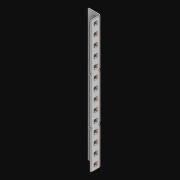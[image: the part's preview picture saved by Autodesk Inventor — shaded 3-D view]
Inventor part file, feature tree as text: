
AUTODESK INVENTOR PART (.ipt)
format: ipt  version: 2021 (Build 250183000, 183)  size: 1,149,440 bytes
history: native  units: in
note: dims shown in document units (in); Inventor stores cm internally (conversion verified against a paired STEP export)
features: extrude x30, other x28, sketch x4, pattern_linear x2, sheet_metal_op x1
ambient origin geometry x8: Origin, YZ Plane, XZ Plane, XY Plane, X Axis, Y Axis, Z Axis, Center Point
bodies: Solid1 (feature_tree)
feature tree (65):
  pattern_linear  "Rectangular Pattern1"  Spacing1=0.5in  [1 undecoded]
  pattern_linear  "Rectangular Pattern3"  Count1=14  [1 undecoded]
  extrude  "Extrusion1"  Depth=0.5in
  extrude  "Extrusion2"  Depth=0.5in
  sketch  "Sketch1"  dims[d0=0.182in]
  other  "Srf1"
  sketch  "Sketch3"  dims[d1=0.063in d2=0.0in]
  other  "Srf3"
  other  "Srf4"
  other  "Srf5"
  other  "Srf6"
  other  "Srf7"
  other  "Srf8"
  other  "Srf9"
  other  "Srf10"
  other  "Srf11"
  other  "Srf12"
  other  "Srf13"
  other  "Srf14"
  other  "Srf15"
  other  "Srf16"
  other  "Srf142"
  other  "Srf143"
  other  "Srf144"
  other  "Srf145"
  other  "Srf146"
  other  "Srf147"
  other  "Srf148"
  other  "Srf149"
  other  "Srf150"
  other  "Srf151"
  other  "Srf152"
  other  "Srf153"
  other  "Srf154"
  sketch  "Sketch4"  dims[d6=0.182in]
  sketch  "Sketch5"  dims[d7=0.063in d8=0.0in d11=0.5in d12=0.3937in d14=0.5in d18=5.5118in d20=0.5in d21=10.5in d22=0.0in d23=0.841in d24=0.0in]
  sheet_metal_op  "Fold1"
  extrude  "ExtrusionSrf1"  TaperAngle=0.0deg  [1 undecoded]
  extrude  "ExtrusionSrf3"  Depth=0.5in TaperAngle=0.0deg
  extrude  "ExtrusionSrf4"  [1 undecoded]
  extrude  "ExtrusionSrf5"  [1 undecoded]
  extrude  "ExtrusionSrf6"  [1 undecoded]
  extrude  "ExtrusionSrf7"  [1 undecoded]
  extrude  "ExtrusionSrf8"  [1 undecoded]
  extrude  "ExtrusionSrf9"  [1 undecoded]
  extrude  "ExtrusionSrf10"  [1 undecoded]
  extrude  "ExtrusionSrf11"  [1 undecoded]
  extrude  "ExtrusionSrf12"  [1 undecoded]
  extrude  "ExtrusionSrf13"  [1 undecoded]
  extrude  "ExtrusionSrf14"  [1 undecoded]
  extrude  "ExtrusionSrf15"  [1 undecoded]
  extrude  "ExtrusionSrf16"  [1 undecoded]
  extrude  "ExtrusionSrf142"  [1 undecoded]
  extrude  "ExtrusionSrf143"  [1 undecoded]
  extrude  "ExtrusionSrf144"  [1 undecoded]
  extrude  "ExtrusionSrf145"  [1 undecoded]
  extrude  "ExtrusionSrf146"  [1 undecoded]
  extrude  "ExtrusionSrf147"  [1 undecoded]
  extrude  "ExtrusionSrf148"  [1 undecoded]
  extrude  "ExtrusionSrf149"  [1 undecoded]
  extrude  "ExtrusionSrf150"  [1 undecoded]
  extrude  "ExtrusionSrf151"  [1 undecoded]
  extrude  "ExtrusionSrf152"  [1 undecoded]
  extrude  "ExtrusionSrf153"  [1 undecoded]
  extrude  "ExtrusionSrf154"  [1 undecoded]
note: 29 required parameter values undecoded (feature->parameter linkage not recoverable at this tier; creation-order binding heuristic only, values carry confidence <= 0.55)
